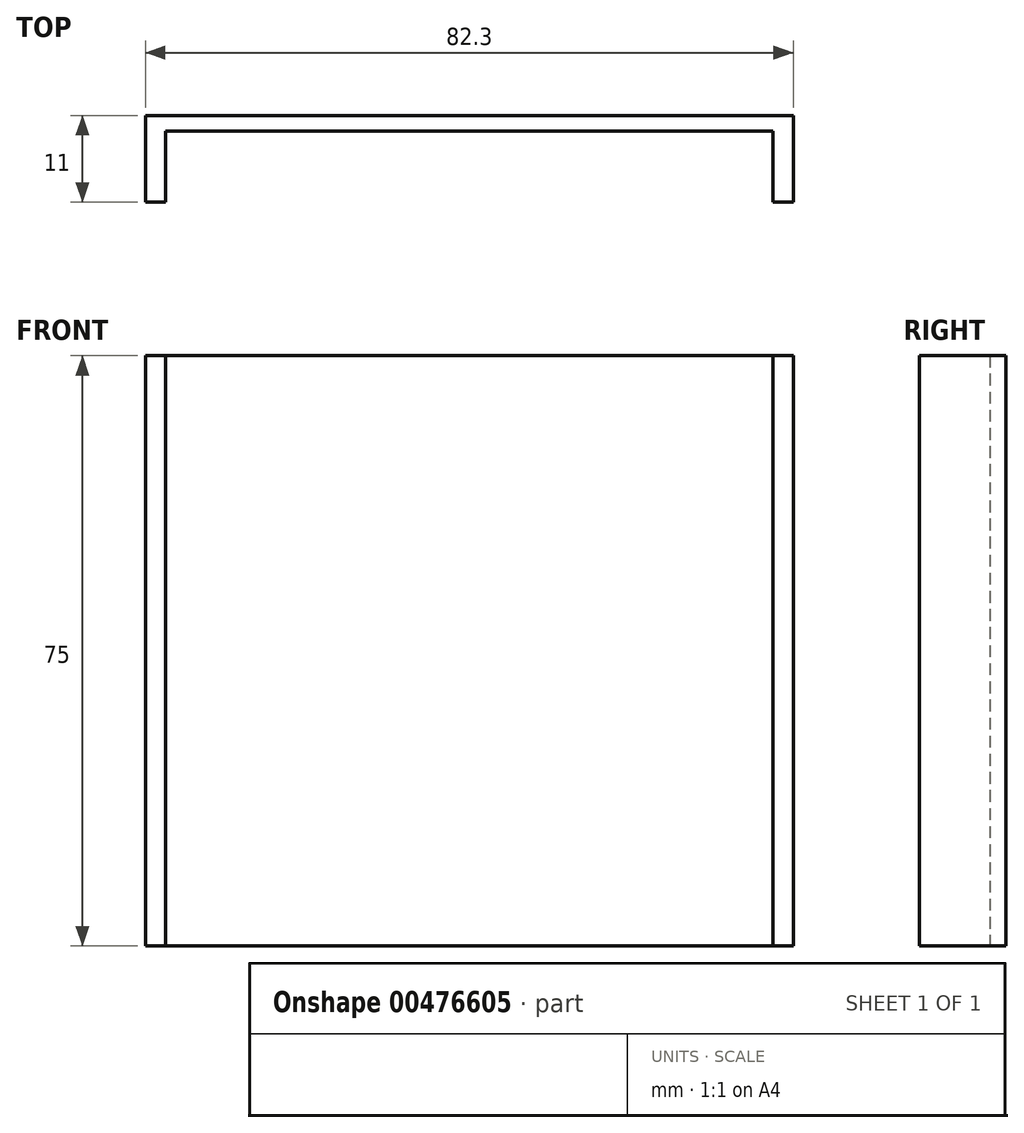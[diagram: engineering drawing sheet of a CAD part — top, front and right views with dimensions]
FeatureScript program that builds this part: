
annotation { "Feature Type Name" : "Feature", "Feature Type Description" : "" }
export const myFeature = defineFeature(function(context is Context, id is Id, definition is map)
    precondition{}
    {
        {
            var Q0;
            Q0=qCreatedBy(makeId("Top.planeOp"),FACE);
            var sketch = newSketch(context, id + "F0", { "sketchPlane" : qUnion([Q0])});
            skLineSegment(sketch, "E0.bottom", {"start": v(-20.06, 3.7) * mm, "end": v(62.24, 3.7) * mm});
            skLineSegment(sketch, "E0.top", {"start": v(-20.06, -7.3) * mm, "end": v(-17.51, -7.3) * mm});
            skLineSegment(sketch, "E0.left", {"start": v(-20.06, 3.7) * mm, "end": v(-20.06, -7.3) * mm});
            skLineSegment(sketch, "E0.right", {"start": v(62.24, 3.7) * mm, "end": v(62.24, -7.3) * mm});
            skLineSegment(sketch, "E1.bottom", {"start": v(-20.06, 3.7) * mm, "end": v(-17.51, 3.7) * mm});
            skLineSegment(sketch, "E1.right", {"start": v(-17.51, 1.7) * mm, "end": v(-17.51, -7.3) * mm});
            skLineSegment(sketch, "E2.bottom", {"start": v(62.24, 3.7) * mm, "end": v(59.69, 3.7) * mm});
            skLineSegment(sketch, "E2.top", {"start": v(62.24, -7.3) * mm, "end": v(59.69, -7.3) * mm});
            skLineSegment(sketch, "E2.right", {"start": v(59.69, 1.7) * mm, "end": v(59.69, -7.3) * mm});
            skLineSegment(sketch, "E3.bottom", {"start": v(-17.51, 3.7) * mm, "end": v(59.69, 3.7) * mm});
            skLineSegment(sketch, "E3.top", {"start": v(-17.51, 1.7) * mm, "end": v(59.69, 1.7) * mm});
            skPoint(sketch, "E4.oppositeSnap0", {"position": v(59.69, 2.7) * mm});
            skLineSegment(sketch, "E4.left", {"start": v(59.69, 2.7) * mm, "end": v(59.69, 2.7) * mm});
            skLineSegment(sketch, "E4.right", {"start": v(61.69, 2.7) * mm, "end": v(61.69, 2.7) * mm});
            skLineSegment(sketch, "E5.trimOffspring", {"start": v(59.69, -7.3) * mm, "end": v(62.24, -7.3) * mm});
            skSolve(sketch);
        }
        {
            var Q0;
            Q0 = qSketchRegion(id + "F0", true);
            extrude(context, id + "F1", {"entities" : qUnion([Q0]), "depth" : 75 * mm});
        }
    });
